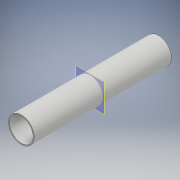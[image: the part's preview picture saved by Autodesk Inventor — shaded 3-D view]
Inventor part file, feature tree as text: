
AUTODESK INVENTOR PART (.ipt)
format: ipt  version: 2017 (Build 210142000, 142)  size: 96,768 bytes
history: native  units: mm
features: extrude x1, sketch x1
ambient origin geometry x8: Origin, YZ Plane, XZ Plane, XY Plane, X Axis, Y Axis, Z Axis, Center Point
bodies: Solid1 (feature_tree)
feature tree (2):
  extrude  "Extrusion1"  Depth=117.0mm
  sketch  "Sketch2"  dims[d0=22.0mm d1=1.0mm d2=117.0mm d3=0.0mm]
